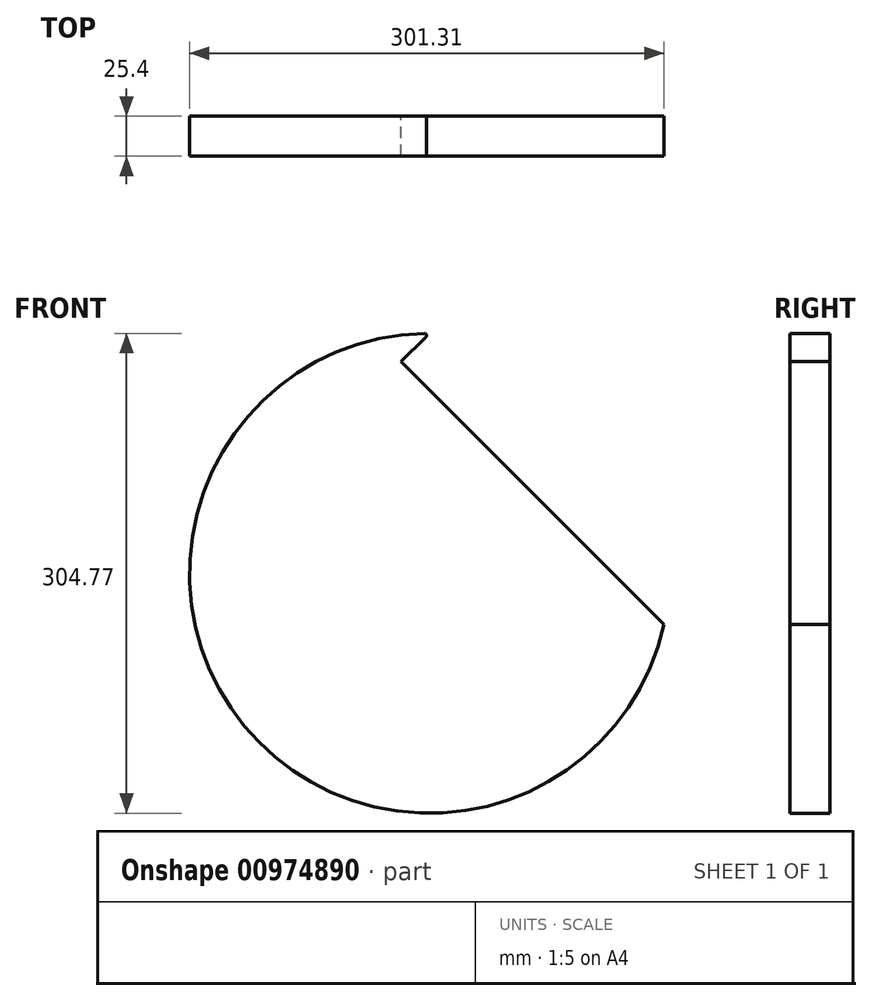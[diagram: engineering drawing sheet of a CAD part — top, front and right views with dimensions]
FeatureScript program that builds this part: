
annotation { "Feature Type Name" : "Feature", "Feature Type Description" : "" }
export const myFeature = defineFeature(function(context is Context, id is Id, definition is map)
    precondition{}
    {
        {
            var Q0;
            Q0=qCreatedBy(makeId("Front.planeOp"),FACE);
            var sketch = newSketch(context, id + "F0", { "sketchPlane" : qUnion([Q0])});
            skCircle(sketch, "E0", {"center": v(0, 0) * mm, "radius": 152.4 * mm});
            skLineSegment(sketch, "E1", {"start": v(0, 152.4) * mm, "end": v(-17.96, 134.44) * mm});
            skLineSegment(sketch, "E2", {"start": v(-17.96, 134.44) * mm, "end": v(148.9, -32.43) * mm});
            skLineSegment(sketch, "E3", {"start": v(0, 152.4) * mm, "end": v(-25.4, 152.4) * mm, "construction": true});
            skSolve(sketch);
        }
        {
            var Q0;
            {var subQ0=sQuery(id+"F0.wireOp",EDGE,"E1");Q0=makeQuery(id+"F0.imprint","IMPRINT",FACE,{"disambiguationData":[TD([[makeQuery(id+"F0.imprint","IMPRINT",EDGE,{"derivedFrom":subQ0}),-1.0]])]});}
            extrude(context, id + "F1", {"entities" : qUnion([Q0]), "depth" : 25.4 * mm, "offsetDistance" : 25.4 * mm});
        }
        {
            var Q0;
            Q0=makeQuery(id+"F1.opExtrude","SWEPT_EDGE",EDGE,{"disambiguationData":[OSD([sQuery(id+"F0.wireOp",EDGE,"E0"),sQuery(id+"F0.wireOp",EDGE,"E1")])]});
            fillet(context, id + "F2", {"entities" : qUnion([Q0]), "radius" : 1.27 * mm, "tangentPropagation" : true, "allowEdgeOverflow" : false});
        }
    });
